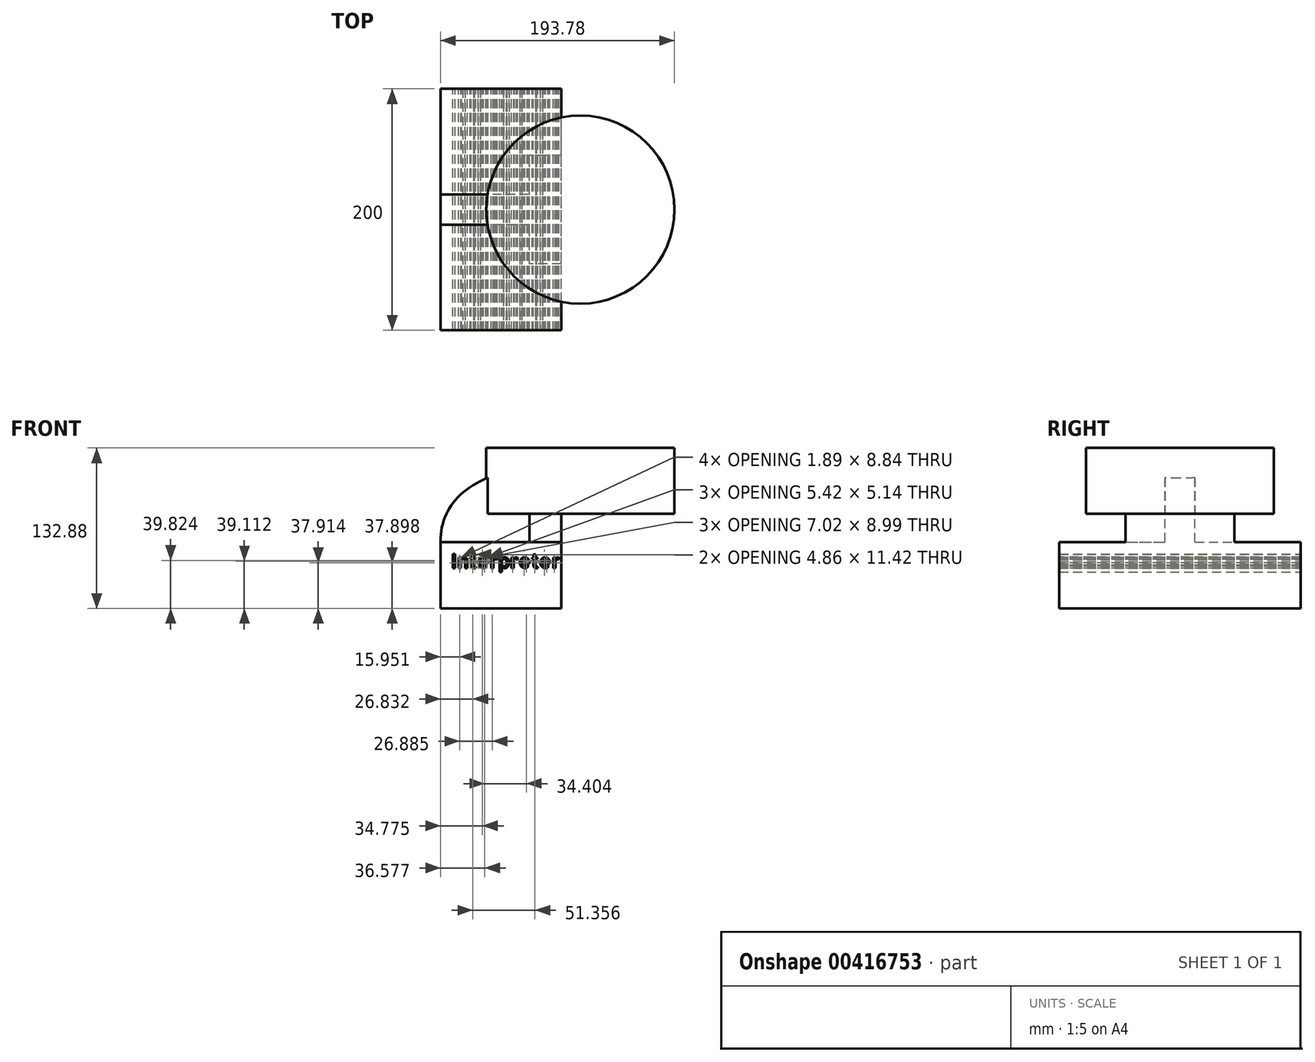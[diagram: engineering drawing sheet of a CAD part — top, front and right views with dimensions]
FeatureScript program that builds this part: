
annotation { "Feature Type Name" : "Feature", "Feature Type Description" : "" }
export const myFeature = defineFeature(function(context is Context, id is Id, definition is map)
    precondition{}
    {
        {
            var Q0;
            Q0=qCreatedBy(makeId("Front.planeOp"),FACE);
            var sketch = newSketch(context, id + "F0", { "sketchPlane" : qUnion([Q0])});
            skLineSegment(sketch, "E0.bottom", {"start": v(50, -27.5) * mm, "end": v(-50, -27.5) * mm});
            skLineSegment(sketch, "E0.top", {"start": v(50, 27.5) * mm, "end": v(-50, 27.5) * mm});
            skLineSegment(sketch, "E0.left", {"start": v(50, -27.5) * mm, "end": v(50, 27.5) * mm});
            skLineSegment(sketch, "E0.right", {"start": v(-50, -27.5) * mm, "end": v(-50, 27.5) * mm});
            skPoint(sketch, "E0.middle", {"position": v(0, 0) * mm});
            skLineSegment(sketch, "E1.bottom", {"start": v(143.78, 51.03) * mm, "end": v(65.87, 51.03) * mm});
            skLineSegment(sketch, "E1.top", {"start": v(143.78, 105.38) * mm, "end": v(65.87, 105.38) * mm});
            skLineSegment(sketch, "E1.left", {"start": v(143.78, 51.03) * mm, "end": v(143.78, 105.38) * mm});
            skLineSegment(sketch, "E1.right", {"start": v(65.87, 51.03) * mm, "end": v(65.87, 105.38) * mm});
            skPoint(sketch, "E1.middle", {"position": v(104.82, 78.2) * mm});
            skLineSegment(sketch, "E2", {"start": v(50, 27.5) * mm, "end": v(50, 51.03) * mm});
            skArc(sketch, "E3", {"start": v(50, 51.03) * mm, "mid": v(54.65, 62.25) * mm, "end": v(65.87, 66.9) * mm});
            skLineSegment(sketch, "E4", {"start": v(65.87, 66.9) * mm, "end": v(108.15, 66.9) * mm});
            skLineSegment(sketch, "E5.0", {"start": v(65.87, 93.32) * mm, "end": v(108.15, 93.32) * mm});
            skArc(sketch, "E5.1", {"start": v(23.58, 51.03) * mm, "mid": v(35.97, 80.94) * mm, "end": v(65.87, 93.32) * mm});
            skLineSegment(sketch, "E5.2", {"start": v(23.58, 27.5) * mm, "end": v(23.58, 51.03) * mm});
            skLineSegment(sketch, "E6", {"start": v(108.15, 93.32) * mm, "end": v(108.15, 66.9) * mm});
            skLineSegment(sketch, "E7", {"start": v(108.15, 93.32) * mm, "end": v(108.15, 105.38) * mm});
            skLineSegment(sketch, "E8", {"start": v(108.15, 66.9) * mm, "end": v(108.15, 51.03) * mm});
            skFitSpline(sketch, "E9", {"points": [v(-50, 27.5) * mm, v(65.87, 93.32) * mm], "startDerivative": vector(-0.9, 125.73) * mm, "endDerivative": vector(228.73, 1.38) * mm});
            skText(sketch, "E10", { "text": "Interpreter", "fontName": "AllertaStencil-Regular.ttf"});
            const initialGuessF0  = {"E10": [-0.04117, 0.00598, 1, 0, 0.01155]};
            skSetInitialGuess(sketch, initialGuessF0);
            skSolve(sketch);
        }
        {
            var Q0;
            Q0=makeQuery(id+"F0.imprint","IMPRINT",FACE,{"disambiguationData":[TD([[makeQuery(id+"F0.imprint","IMPRINT",EDGE,{"derivedFrom":sQuery(id+"F0.wireOp",EDGE,"E0.bottom")}),-1.0]])]});
            extrude(context, id + "F1", {"entities" : qUnion([Q0]), "endBound" : BoundingType.SYMMETRIC, "depth" : 200 * mm});
        }
        {
            var Q0;
            {var subQ1=sQuery(id+"F0.wireOp",EDGE,"E2");Q0=makeQuery(id+"F0.imprint","IMPRINT",FACE,{"disambiguationData":[TD([[makeQuery(id+"F0.imprint","IMPRINT",EDGE,{"derivedFrom":subQ1}),1.0]])]});}
            extrude(context, id + "F2", {"entities" : qUnion([Q0]), "operationType" : NewBodyOperationType.ADD, "endBound" : BoundingType.SYMMETRIC, "depth" : 90 * mm});
        }
        {
            var Q0;
            {var subQ3=sQuery(id+"F0.wireOp",EDGE,"E5.2");Q0=makeQuery(id+"F0.imprint","IMPRINT",FACE,{"disambiguationData":[TD([[makeQuery(id+"F0.imprint","IMPRINT",EDGE,{"derivedFrom":subQ3}),1.0]])]});}
            extrude(context, id + "F3", {"entities" : qUnion([Q0]), "operationType" : NewBodyOperationType.ADD, "endBound" : BoundingType.SYMMETRIC, "depth" : 25 * mm});
        }
        {
            var Q0;
            {var subQ0=sQuery(id+"F0.wireOp",EDGE,"E1.left");Q0=makeQuery(id+"F0.imprint","IMPRINT",FACE,{"disambiguationData":[TD([[makeQuery(id+"F0.imprint","IMPRINT",EDGE,{"derivedFrom":subQ0}),1.0]])]});}
            var Q1;
            {var subQ0=sQuery(id+"F0.wireOp",EDGE,"E4");Q1=makeQuery(id+"F0.imprint","IMPRINT",FACE,{"disambiguationData":[TD([[makeQuery(id+"F0.imprint","IMPRINT",EDGE,{"derivedFrom":subQ0}),1.0]])]});}
            var Q2;
            {var subQ4=sQuery(id+"F0.wireOp",EDGE,"E4");Q2=makeQuery(id+"F0.imprint","IMPRINT",FACE,{"disambiguationData":[TD([[makeQuery(id+"F0.imprint","IMPRINT",EDGE,{"derivedFrom":subQ4}),-1.0]])]});}
            var Q3;
            {var subQ4=sQuery(id+"F0.wireOp",EDGE,"E5.0");Q3=makeQuery(id+"F0.imprint","IMPRINT",FACE,{"disambiguationData":[TD([[makeQuery(id+"F0.imprint","IMPRINT",EDGE,{"derivedFrom":subQ4}),1.0]])]});}
            var Q4;
            Q4=sQuery(id+"F0.wireOp",EDGE,"E1.right");
            revolve(context, id + "F4", {"operationType" : NewBodyOperationType.ADD, "entities" : qUnion([Q0, Q1, Q2, Q3]), "axis" : qUnion([Q4]), "revolveType" : RevolveType.FULL});
        }
    });
